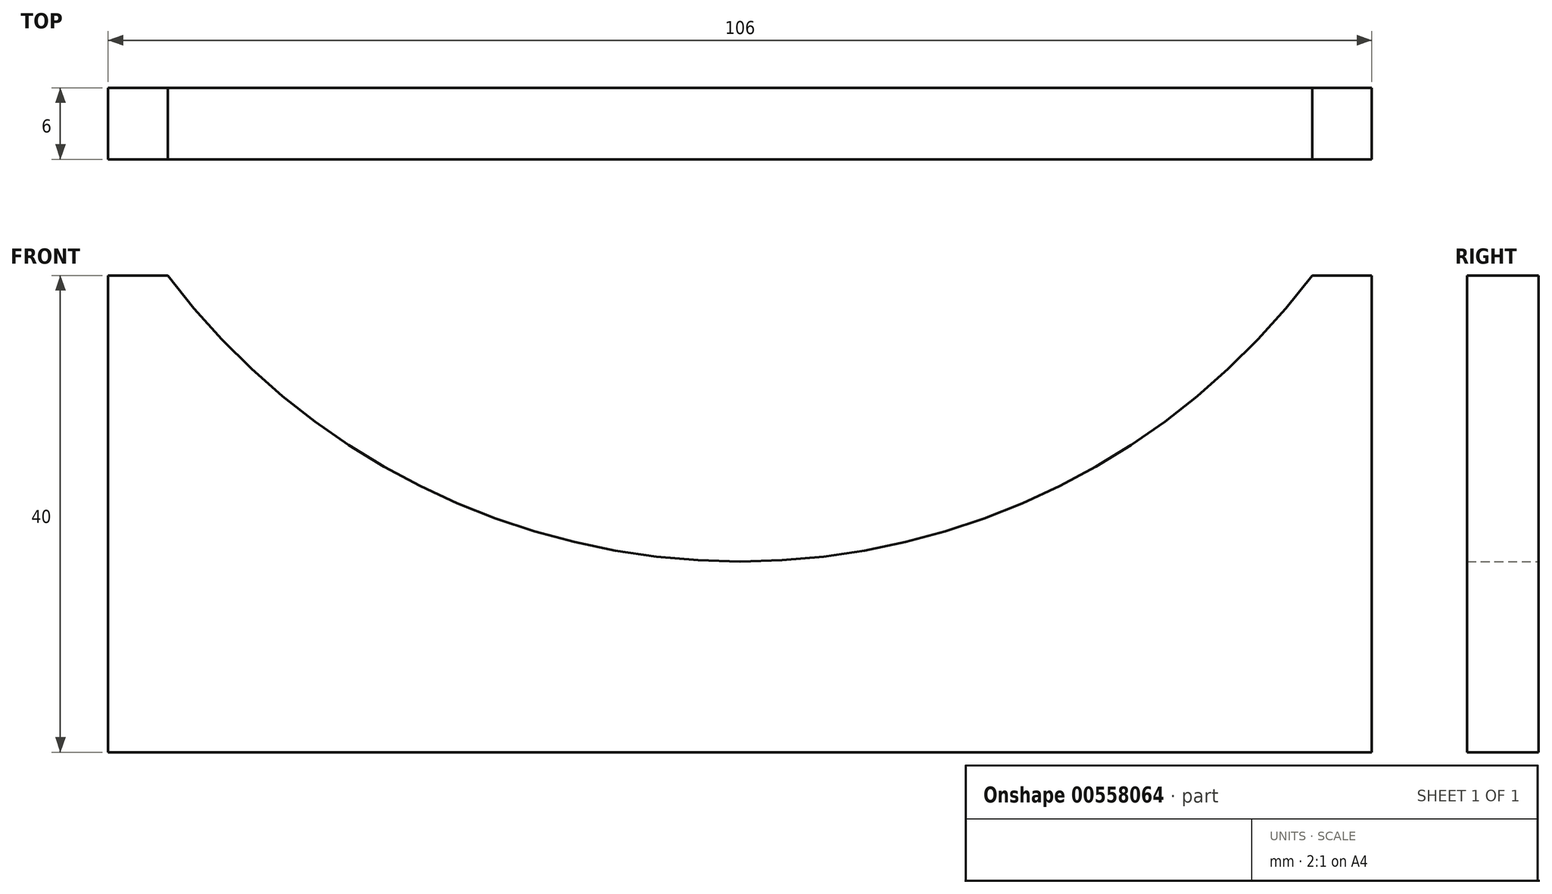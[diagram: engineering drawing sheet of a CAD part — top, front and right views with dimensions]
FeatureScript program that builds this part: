
annotation { "Feature Type Name" : "Feature", "Feature Type Description" : "" }
export const myFeature = defineFeature(function(context is Context, id is Id, definition is map)
    precondition{}
    {
        {
            var Q0;
            Q0=qCreatedBy(makeId("Front.planeOp"),FACE);
            var sketch = newSketch(context, id + "F0", { "sketchPlane" : qUnion([Q0])});
            skLineSegment(sketch, "E0", {"start": v(0, 0) * mm, "end": v(0, 40) * mm});
            skLineSegment(sketch, "E1", {"start": v(0, 40) * mm, "end": v(5, 40) * mm});
            skLineSegment(sketch, "E2", {"start": v(0, 0) * mm, "end": v(106, 0) * mm});
            skLineSegment(sketch, "E3", {"start": v(106, 0) * mm, "end": v(106, 40) * mm});
            skLineSegment(sketch, "E4", {"start": v(106, 40) * mm, "end": v(101, 40) * mm});
            skArc(sketch, "E5", {"start": v(5, 40) * mm, "mid": v(53, 16) * mm, "end": v(101, 40) * mm});
            skSolve(sketch);
        }
        {
            var Q0;
            Q0=makeQuery(id+"F0.imprint","IMPRINT",FACE,{"disambiguationData":[TD([[makeQuery(id+"F0.imprint","IMPRINT",EDGE,{"derivedFrom":sQuery(id+"F0.wireOp",EDGE,"E0")}),-1.0]])]});
            extrude(context, id + "F1", {"entities" : qUnion([Q0]), "endBound" : BoundingType.SYMMETRIC, "depth" : 6 * mm, "offsetDistance" : 25 * mm});
        }
    });
